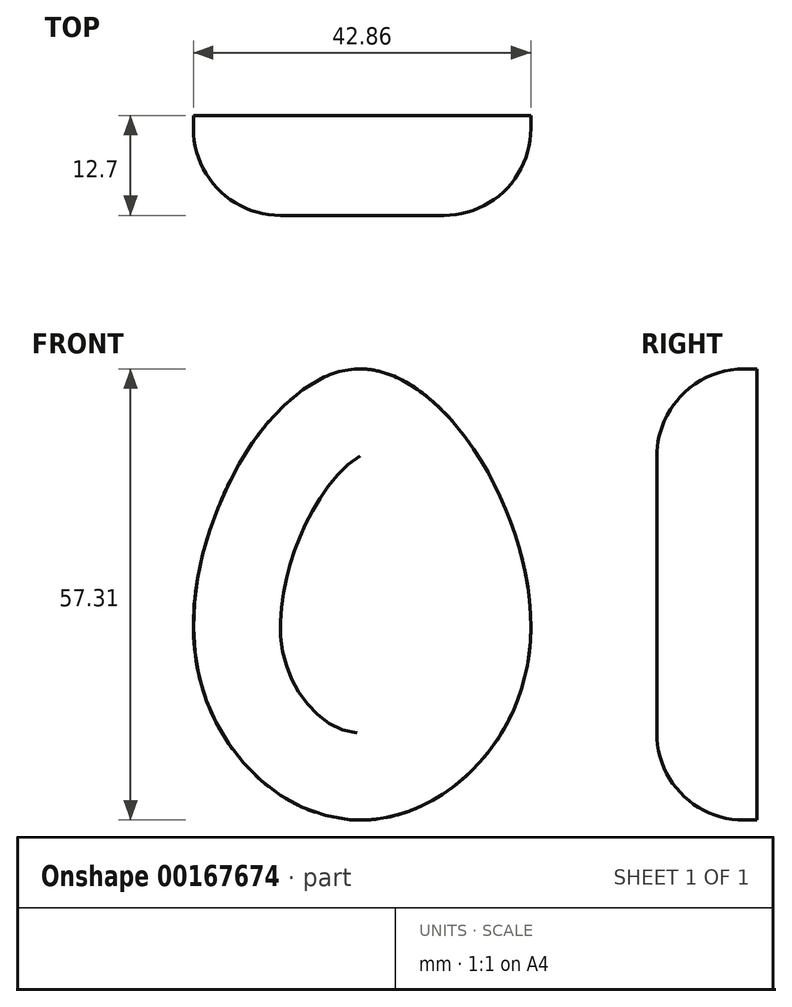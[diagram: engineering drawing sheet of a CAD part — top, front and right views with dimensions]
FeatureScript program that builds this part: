
annotation { "Feature Type Name" : "Feature", "Feature Type Description" : "" }
export const myFeature = defineFeature(function(context is Context, id is Id, definition is map)
    precondition{}
    {
        {
            var Q0;
            Q0=qCreatedBy(makeId("Front.planeOp"),FACE);
            var sketch = newSketch(context, id + "F0", { "sketchPlane" : qUnion([Q0])});
            skFitSpline(sketch, "E0", {"points": [v(21.7, 0) * mm, v(0, 34.62) * mm, v(-21.04, 0) * mm, v(0, -22.7) * mm, v(21.7, 0) * mm]});
            skSolve(sketch);
        }
        {
            var Q0;
            Q0 = qSketchRegion(id + "F0", true);
            extrude(context, id + "F1", {"entities" : qUnion([Q0]), "depth" : 12.7 * mm});
        }
        {
            var Q0;
            Q0=makeQuery(id+"F1.opExtrude","CAP_EDGE",EDGE,{"disambiguationData":[OSD([sQuery(id+"F0.wireOp",EDGE,"E0")])],"isStart":false});
            fillet(context, id + "F2", {"entities" : qUnion([Q0]), "radius" : 11.04 * mm, "tangentPropagation" : true, "allowEdgeOverflow" : false});
        }
    });
